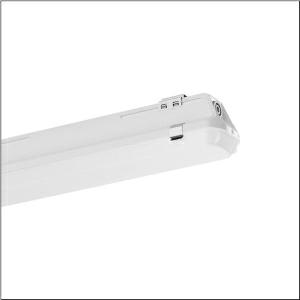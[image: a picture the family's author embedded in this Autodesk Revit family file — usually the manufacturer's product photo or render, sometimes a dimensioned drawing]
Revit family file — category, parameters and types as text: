
# Revit family: monsun_r__11_51fp209p460h_6055
name_source: partatom
category: Lighting Fixtures
units: mm (PartAtom-declared; Revit-internal decimal feet)

## family parameters
Cut with Voids When Loaded = No
Host = Face
Light Source = No
Part Type = Normal
Room Calculation Point = No
Round Connector Dimension = Use Diameter
Shared = No

## types (1)
- Monsun® 11 (1 x LED, 5490 lm, 34 W, 4000K)
    Apparent Load = 34 VA
    CIE Flux Codes = 45 75 93 94 100
    Color Rendering = 80
    Color Temperature = 4000K
    Default Elevation = 1800 mm
    Description = Monsun® 11, damp-proof luminaire, chain hanger, primary optical cover: enclosure, of PC, light emission: direct distribution, primary light characteristic: symmetric, installation type: suspended mounting, surface-mounted, horizontal mounting, vertical mounting, LED, rated luminous flux: 5.490lm, luminous efficacy: 161lm/W, light colour: 840, colour temperature: 4000K, control gear: ECG, with terminal, 3-pole, max. 2.5mm², mains connection: 220..240V, AC, 50/60Hz, rated input power: 34W, luminaire housing, of glass-fibre reinforced polyester, uncoated, bright grey, incl. chain hanger, length: 1.590mm, width: 90mm, height: 88mm, clip for enclosure, of stainless steel (V2A), ceiling mounting element, of stainless steel (V2A), chain hanger, of stainless steel (V2A), protection rating (complete): IP66, insulation class (complete): insulation class I (protective earthing), certification: CE, ENEC, VDE, UKCA, protection symbol: D, impact resistance: IK08, permissible operating ambient temperature: -35..+40°C, standard: EN 50419, EN 60598-2-1, no direct snow, no direct sun, no direct rain, for indoor or canopied outdoor use, corresponds to IFS (International Featured Standards) requirements for safety and quality in the food industry, contact your sales advisor before using the luminaires in applications with unclear chemical exposure, large temperature fluctuations or condensation-forming humidity, LABS conformity tested according to VDMA 24364:2018-05, packaging unit: 1 piece
    Height = 89 mm
    Lamp = 1 x LED
    Lamp Light Flux = 5490 lm
    Lamp Power = 34 W
    Lamp count = 1
    Length = 1590 mm
    Luminous efficacy = 161 lm/W
    Manufacturer = Siteco
    ModVariant = No
    Model = 51FP209P460H
    Mounting Place = Ceiling
    Mounting Type = Surface mounted
    Number of Poles = 1
    OnlyDefault = Yes
    Power Factor = 1
    Product Name = Monsun® 11
    Product group = damp-proof luminaire
    ProductGroupID = 300
    Protection Class = Protection class I
    Protection Degree = IP 66
    RLX_Detail_Level = 1
    RLX_Emergency_Light_Flux = 0 lm
    RLX_Emergency_Type = 0
    RLX_Emergency_Type_DB = No
    RlxData = <blob elided: 88661 chars, md5=2b97496e>
    Socket = socket
    Standby Power = 0 W
    System Light Flux = 5490 lm
    System Power = 34 W
    Type Comments = Product without accessories
    Type Image = l_1004748.jpg
    URL = http://relux.com
    VarID = ---
    Voltage = 0 V
    Weight = 0.00 kg
    Width = 90 mm

## geometry (parser evidence)
native form markers: Blend x4, Sweep x12
no freeform markers — native parametric forms only
